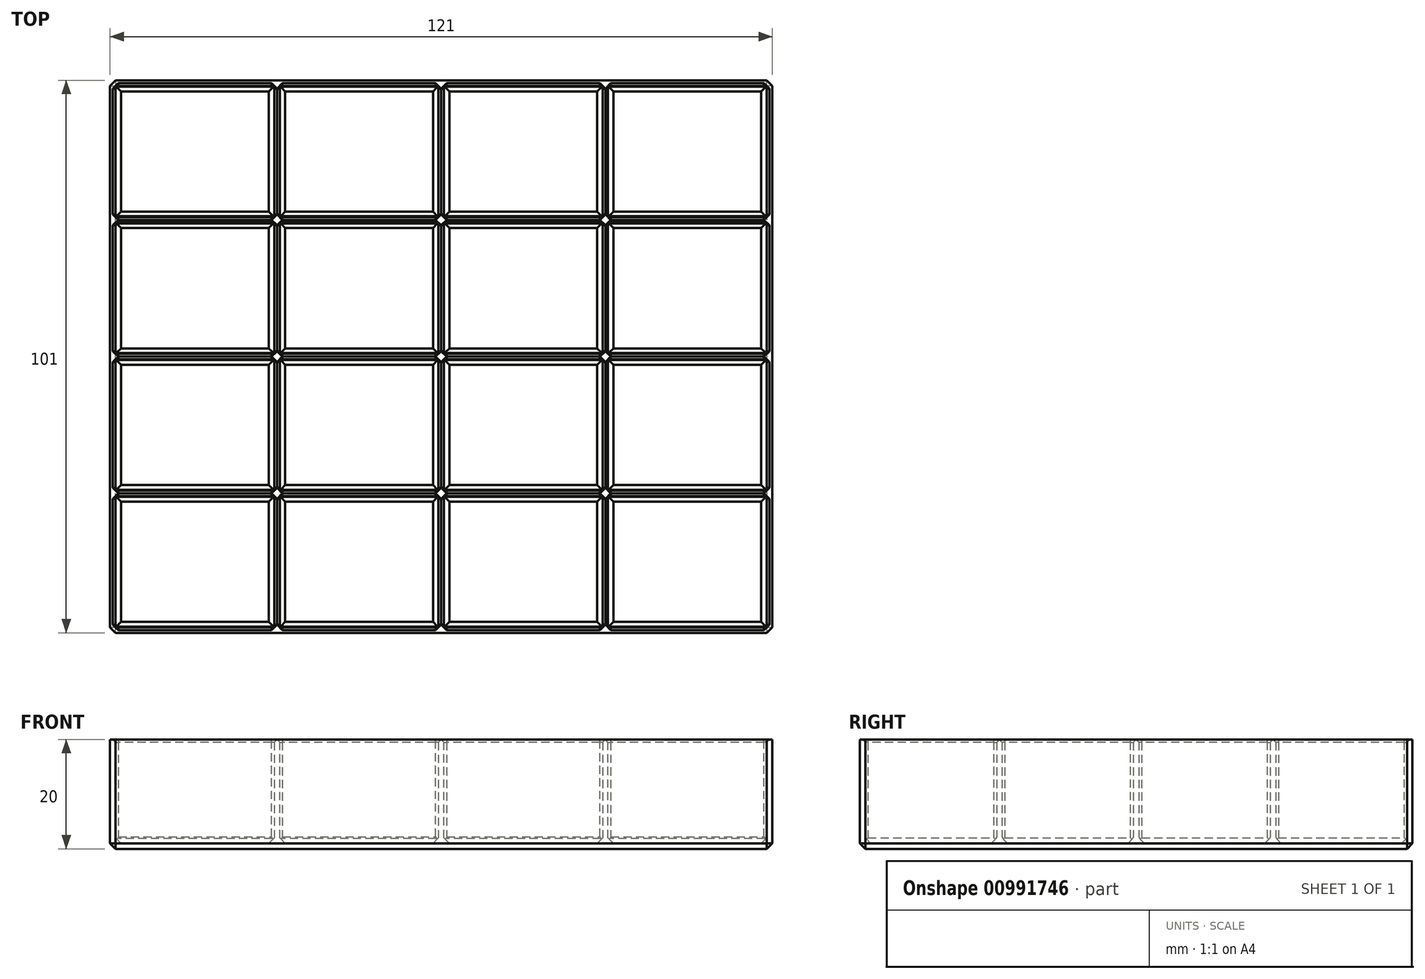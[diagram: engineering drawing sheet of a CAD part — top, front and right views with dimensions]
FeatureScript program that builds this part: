
annotation { "Feature Type Name" : "Feature", "Feature Type Description" : "" }
export const myFeature = defineFeature(function(context is Context, id is Id, definition is map)
    precondition{}
    {
        {
            var Q0;
            Q0=qCreatedBy(makeId("Top.planeOp"),FACE);
            var sketch = newSketch(context, id + "F0", { "sketchPlane" : qUnion([Q0])});
            skLineSegment(sketch, "E0.bottom", {"start": v(-60, 50) * mm, "end": v(60, 50) * mm, "construction": true});
            skLineSegment(sketch, "E0.top", {"start": v(-60, -50) * mm, "end": v(60, -50) * mm, "construction": true});
            skLineSegment(sketch, "E0.left", {"start": v(-60, 50) * mm, "end": v(-60, -50) * mm, "construction": true});
            skLineSegment(sketch, "E0.right", {"start": v(60, 50) * mm, "end": v(60, -50) * mm, "construction": true});
            skLineSegment(sketch, "E1", {"start": v(0, 50) * mm, "end": v(0, -50) * mm, "construction": true});
            skLineSegment(sketch, "E2", {"start": v(-60, 0) * mm, "end": v(60, 0) * mm, "construction": true});
            skLineSegment(sketch, "E3", {"start": v(-30, 50) * mm, "end": v(-30, -50) * mm, "construction": true});
            skLineSegment(sketch, "E4", {"start": v(30, 50) * mm, "end": v(30, -50) * mm, "construction": true});
            skLineSegment(sketch, "E5", {"start": v(60, -25) * mm, "end": v(-60, -25) * mm, "construction": true});
            skLineSegment(sketch, "E6", {"start": v(60, 25) * mm, "end": v(-60, 25) * mm, "construction": true});
            skLineSegment(sketch, "E7.bottom", {"start": v(-59.5, 49.5) * mm, "end": v(-30.5, 49.5) * mm});
            skLineSegment(sketch, "E7.top", {"start": v(-59.5, 25.5) * mm, "end": v(-30.5, 25.5) * mm});
            skLineSegment(sketch, "E7.left", {"start": v(-59.5, 49.5) * mm, "end": v(-59.5, 25.5) * mm});
            skLineSegment(sketch, "E7.right", {"start": v(-30.5, 49.5) * mm, "end": v(-30.5, 25.5) * mm});
            skLineSegment(sketch, "E8.0.1.0", {"start": v(-59.5, 24.5) * mm, "end": v(-30.5, 24.5) * mm});
            skLineSegment(sketch, "E8.0.1.1", {"start": v(-59.5, 24.5) * mm, "end": v(-59.5, 0.5) * mm});
            skLineSegment(sketch, "E8.0.1.2", {"start": v(-59.5, 0.5) * mm, "end": v(-30.5, 0.5) * mm});
            skLineSegment(sketch, "E8.0.1.3", {"start": v(-30.5, 24.5) * mm, "end": v(-30.5, 0.5) * mm});
            skLineSegment(sketch, "E8.0.2.0", {"start": v(-59.5, -0.5) * mm, "end": v(-30.5, -0.5) * mm});
            skLineSegment(sketch, "E8.0.2.1", {"start": v(-59.5, -0.5) * mm, "end": v(-59.5, -24.5) * mm});
            skLineSegment(sketch, "E8.0.2.2", {"start": v(-59.5, -24.5) * mm, "end": v(-30.5, -24.5) * mm});
            skLineSegment(sketch, "E8.0.2.3", {"start": v(-30.5, -0.5) * mm, "end": v(-30.5, -24.5) * mm});
            skLineSegment(sketch, "E8.0.3.0", {"start": v(-59.5, -25.5) * mm, "end": v(-30.5, -25.5) * mm});
            skLineSegment(sketch, "E8.0.3.1", {"start": v(-59.5, -25.5) * mm, "end": v(-59.5, -49.5) * mm});
            skLineSegment(sketch, "E8.0.3.2", {"start": v(-59.5, -49.5) * mm, "end": v(-30.5, -49.5) * mm});
            skLineSegment(sketch, "E8.0.3.3", {"start": v(-30.5, -25.5) * mm, "end": v(-30.5, -49.5) * mm});
            skLineSegment(sketch, "E8.1.0.0", {"start": v(-29.5, 49.5) * mm, "end": v(-0.5, 49.5) * mm});
            skLineSegment(sketch, "E8.1.0.1", {"start": v(-29.5, 49.5) * mm, "end": v(-29.5, 25.5) * mm});
            skLineSegment(sketch, "E8.1.0.2", {"start": v(-29.5, 25.5) * mm, "end": v(-0.5, 25.5) * mm});
            skLineSegment(sketch, "E8.1.0.3", {"start": v(-0.5, 49.5) * mm, "end": v(-0.5, 25.5) * mm});
            skLineSegment(sketch, "E8.1.1.0", {"start": v(-29.5, 24.5) * mm, "end": v(-0.5, 24.5) * mm});
            skLineSegment(sketch, "E8.1.1.1", {"start": v(-29.5, 24.5) * mm, "end": v(-29.5, 0.5) * mm});
            skLineSegment(sketch, "E8.1.1.2", {"start": v(-29.5, 0.5) * mm, "end": v(-0.5, 0.5) * mm});
            skLineSegment(sketch, "E8.1.1.3", {"start": v(-0.5, 24.5) * mm, "end": v(-0.5, 0.5) * mm});
            skLineSegment(sketch, "E8.1.2.0", {"start": v(-29.5, -0.5) * mm, "end": v(-0.5, -0.5) * mm});
            skLineSegment(sketch, "E8.1.2.1", {"start": v(-29.5, -0.5) * mm, "end": v(-29.5, -24.5) * mm});
            skLineSegment(sketch, "E8.1.2.2", {"start": v(-29.5, -24.5) * mm, "end": v(-0.5, -24.5) * mm});
            skLineSegment(sketch, "E8.1.2.3", {"start": v(-0.5, -0.5) * mm, "end": v(-0.5, -24.5) * mm});
            skLineSegment(sketch, "E8.1.3.0", {"start": v(-29.5, -25.5) * mm, "end": v(-0.5, -25.5) * mm});
            skLineSegment(sketch, "E8.1.3.1", {"start": v(-29.5, -25.5) * mm, "end": v(-29.5, -49.5) * mm});
            skLineSegment(sketch, "E8.1.3.2", {"start": v(-29.5, -49.5) * mm, "end": v(-0.5, -49.5) * mm});
            skLineSegment(sketch, "E8.1.3.3", {"start": v(-0.5, -25.5) * mm, "end": v(-0.5, -49.5) * mm});
            skLineSegment(sketch, "E8.2.0.0", {"start": v(0.5, 49.5) * mm, "end": v(29.5, 49.5) * mm});
            skLineSegment(sketch, "E8.2.0.1", {"start": v(0.5, 49.5) * mm, "end": v(0.5, 25.5) * mm});
            skLineSegment(sketch, "E8.2.0.2", {"start": v(0.5, 25.5) * mm, "end": v(29.5, 25.5) * mm});
            skLineSegment(sketch, "E8.2.0.3", {"start": v(29.5, 49.5) * mm, "end": v(29.5, 25.5) * mm});
            skLineSegment(sketch, "E8.2.1.0", {"start": v(0.5, 24.5) * mm, "end": v(29.5, 24.5) * mm});
            skLineSegment(sketch, "E8.2.1.1", {"start": v(0.5, 24.5) * mm, "end": v(0.5, 0.5) * mm});
            skLineSegment(sketch, "E8.2.1.2", {"start": v(0.5, 0.5) * mm, "end": v(29.5, 0.5) * mm});
            skLineSegment(sketch, "E8.2.1.3", {"start": v(29.5, 24.5) * mm, "end": v(29.5, 0.5) * mm});
            skLineSegment(sketch, "E8.2.2.0", {"start": v(0.5, -0.5) * mm, "end": v(29.5, -0.5) * mm});
            skLineSegment(sketch, "E8.2.2.1", {"start": v(0.5, -0.5) * mm, "end": v(0.5, -24.5) * mm});
            skLineSegment(sketch, "E8.2.2.2", {"start": v(0.5, -24.5) * mm, "end": v(29.5, -24.5) * mm});
            skLineSegment(sketch, "E8.2.2.3", {"start": v(29.5, -0.5) * mm, "end": v(29.5, -24.5) * mm});
            skLineSegment(sketch, "E8.2.3.0", {"start": v(0.5, -25.5) * mm, "end": v(29.5, -25.5) * mm});
            skLineSegment(sketch, "E8.2.3.1", {"start": v(0.5, -25.5) * mm, "end": v(0.5, -49.5) * mm});
            skLineSegment(sketch, "E8.2.3.2", {"start": v(0.5, -49.5) * mm, "end": v(29.5, -49.5) * mm});
            skLineSegment(sketch, "E8.2.3.3", {"start": v(29.5, -25.5) * mm, "end": v(29.5, -49.5) * mm});
            skLineSegment(sketch, "E8.3.0.0", {"start": v(30.5, 49.5) * mm, "end": v(59.5, 49.5) * mm});
            skLineSegment(sketch, "E8.3.0.1", {"start": v(30.5, 49.5) * mm, "end": v(30.5, 25.5) * mm});
            skLineSegment(sketch, "E8.3.0.2", {"start": v(30.5, 25.5) * mm, "end": v(59.5, 25.5) * mm});
            skLineSegment(sketch, "E8.3.0.3", {"start": v(59.5, 49.5) * mm, "end": v(59.5, 25.5) * mm});
            skLineSegment(sketch, "E8.3.1.0", {"start": v(30.5, 24.5) * mm, "end": v(59.5, 24.5) * mm});
            skLineSegment(sketch, "E8.3.1.1", {"start": v(30.5, 24.5) * mm, "end": v(30.5, 0.5) * mm});
            skLineSegment(sketch, "E8.3.1.2", {"start": v(30.5, 0.5) * mm, "end": v(59.5, 0.5) * mm});
            skLineSegment(sketch, "E8.3.1.3", {"start": v(59.5, 24.5) * mm, "end": v(59.5, 0.5) * mm});
            skLineSegment(sketch, "E8.3.2.0", {"start": v(30.5, -0.5) * mm, "end": v(59.5, -0.5) * mm});
            skLineSegment(sketch, "E8.3.2.1", {"start": v(30.5, -0.5) * mm, "end": v(30.5, -24.5) * mm});
            skLineSegment(sketch, "E8.3.2.2", {"start": v(30.5, -24.5) * mm, "end": v(59.5, -24.5) * mm});
            skLineSegment(sketch, "E8.3.2.3", {"start": v(59.5, -0.5) * mm, "end": v(59.5, -24.5) * mm});
            skLineSegment(sketch, "E8.3.3.0", {"start": v(30.5, -25.5) * mm, "end": v(59.5, -25.5) * mm});
            skLineSegment(sketch, "E8.3.3.1", {"start": v(30.5, -25.5) * mm, "end": v(30.5, -49.5) * mm});
            skLineSegment(sketch, "E8.3.3.2", {"start": v(30.5, -49.5) * mm, "end": v(59.5, -49.5) * mm});
            skLineSegment(sketch, "E8.3.3.3", {"start": v(59.5, -25.5) * mm, "end": v(59.5, -49.5) * mm});
            skLineSegment(sketch, "E8.direction1", {"start": v(-59.5, 25.5) * mm, "end": v(-29.5, 25.5) * mm, "construction": true});
            skLineSegment(sketch, "E8.direction2", {"start": v(-59.5, 25.5) * mm, "end": v(-59.5, 0.5) * mm, "construction": true});
            skLineSegment(sketch, "E9.bottom", {"start": v(-60.5, 50.5) * mm, "end": v(60.5, 50.5) * mm});
            skLineSegment(sketch, "E9.top", {"start": v(-60.5, -50.5) * mm, "end": v(60.5, -50.5) * mm});
            skLineSegment(sketch, "E9.left", {"start": v(-60.5, 50.5) * mm, "end": v(-60.5, -50.5) * mm});
            skLineSegment(sketch, "E9.right", {"start": v(60.5, 50.5) * mm, "end": v(60.5, -50.5) * mm});
            skSolve(sketch);
        }
        {
            var Q0;
            Q0 = qSketchRegion(id + "F0", true);
            extrude(context, id + "F1", {"entities" : qUnion([Q0]), "depth" : 19 * mm, "offsetDistance" : 25 * mm});
        }
        {
            var Q0;
            Q0=makeQuery(id+"F0.imprint","IMPRINT",FACE,{"disambiguationData":[TD([[makeQuery(id+"F0.imprint","IMPRINT",EDGE,{"derivedFrom":sQuery(id+"F0.wireOp",EDGE,"E8.0.3.0")}),-1.0]])]});
            var Q1;
            Q1=makeQuery(id+"F0.imprint","IMPRINT",FACE,{"disambiguationData":[TD([[makeQuery(id+"F0.imprint","IMPRINT",EDGE,{"derivedFrom":sQuery(id+"F0.wireOp",EDGE,"E8.1.3.0")}),-1.0]])]});
            var Q2;
            Q2=makeQuery(id+"F0.imprint","IMPRINT",FACE,{"disambiguationData":[TD([[makeQuery(id+"F0.imprint","IMPRINT",EDGE,{"derivedFrom":sQuery(id+"F0.wireOp",EDGE,"E8.2.3.0")}),-1.0]])]});
            var Q3;
            Q3=makeQuery(id+"F0.imprint","IMPRINT",FACE,{"disambiguationData":[TD([[makeQuery(id+"F0.imprint","IMPRINT",EDGE,{"derivedFrom":sQuery(id+"F0.wireOp",EDGE,"E8.3.3.0")}),-1.0]])]});
            var Q4;
            Q4=makeQuery(id+"F0.imprint","IMPRINT",FACE,{"disambiguationData":[TD([[makeQuery(id+"F0.imprint","IMPRINT",EDGE,{"derivedFrom":sQuery(id+"F0.wireOp",EDGE,"E8.3.2.0")}),-1.0]])]});
            var Q5;
            Q5=makeQuery(id+"F0.imprint","IMPRINT",FACE,{"disambiguationData":[TD([[makeQuery(id+"F0.imprint","IMPRINT",EDGE,{"derivedFrom":sQuery(id+"F0.wireOp",EDGE,"E8.2.2.0")}),-1.0]])]});
            var Q6;
            Q6=makeQuery(id+"F0.imprint","IMPRINT",FACE,{"disambiguationData":[TD([[makeQuery(id+"F0.imprint","IMPRINT",EDGE,{"derivedFrom":sQuery(id+"F0.wireOp",EDGE,"E8.1.2.0")}),-1.0]])]});
            var Q7;
            Q7=makeQuery(id+"F0.imprint","IMPRINT",FACE,{"disambiguationData":[TD([[makeQuery(id+"F0.imprint","IMPRINT",EDGE,{"derivedFrom":sQuery(id+"F0.wireOp",EDGE,"E8.0.2.0")}),-1.0]])]});
            var Q8;
            Q8=makeQuery(id+"F0.imprint","IMPRINT",FACE,{"disambiguationData":[TD([[makeQuery(id+"F0.imprint","IMPRINT",EDGE,{"derivedFrom":sQuery(id+"F0.wireOp",EDGE,"E8.0.1.0")}),-1.0]])]});
            var Q9;
            Q9=makeQuery(id+"F0.imprint","IMPRINT",FACE,{"disambiguationData":[TD([[makeQuery(id+"F0.imprint","IMPRINT",EDGE,{"derivedFrom":sQuery(id+"F0.wireOp",EDGE,"E8.1.1.0")}),-1.0]])]});
            var Q10;
            Q10=makeQuery(id+"F0.imprint","IMPRINT",FACE,{"disambiguationData":[TD([[makeQuery(id+"F0.imprint","IMPRINT",EDGE,{"derivedFrom":sQuery(id+"F0.wireOp",EDGE,"E8.2.1.0")}),-1.0]])]});
            var Q11;
            Q11=makeQuery(id+"F0.imprint","IMPRINT",FACE,{"disambiguationData":[TD([[makeQuery(id+"F0.imprint","IMPRINT",EDGE,{"derivedFrom":sQuery(id+"F0.wireOp",EDGE,"E8.3.1.0")}),-1.0]])]});
            var Q12;
            Q12=makeQuery(id+"F0.imprint","IMPRINT",FACE,{"disambiguationData":[TD([[makeQuery(id+"F0.imprint","IMPRINT",EDGE,{"derivedFrom":sQuery(id+"F0.wireOp",EDGE,"E8.3.0.0")}),-1.0]])]});
            var Q13;
            Q13=makeQuery(id+"F0.imprint","IMPRINT",FACE,{"disambiguationData":[TD([[makeQuery(id+"F0.imprint","IMPRINT",EDGE,{"derivedFrom":sQuery(id+"F0.wireOp",EDGE,"E8.2.0.0")}),-1.0]])]});
            var Q14;
            Q14=makeQuery(id+"F0.imprint","IMPRINT",FACE,{"disambiguationData":[TD([[makeQuery(id+"F0.imprint","IMPRINT",EDGE,{"derivedFrom":sQuery(id+"F0.wireOp",EDGE,"E8.1.0.0")}),-1.0]])]});
            var Q15;
            Q15=makeQuery(id+"F0.imprint","IMPRINT",FACE,{"disambiguationData":[TD([[makeQuery(id+"F0.imprint","IMPRINT",EDGE,{"derivedFrom":sQuery(id+"F0.wireOp",EDGE,"E7.bottom")}),-1.0]])]});
            var Q16;
            Q16=makeQuery(id+"F0.imprint","IMPRINT",FACE,{"disambiguationData":[TD([[makeQuery(id+"F0.imprint","IMPRINT",EDGE,{"derivedFrom":sQuery(id+"F0.wireOp",EDGE,"E7.bottom")}),1.0]])]});
            extrude(context, id + "F2", {"entities" : qUnion([Q0, Q1, Q2, Q3, Q4, Q5, Q6, Q7, Q8, Q9, Q10, Q11, Q12, Q13, Q14, Q15, Q16]), "operationType" : NewBodyOperationType.ADD, "oppositeDirection" : true, "depth" : 1 * mm, "offsetDistance" : 25 * mm});
        }
        {
            var Q0;
            Q0=makeQuery(id+"F2.opExtrude","CAP_EDGE",EDGE,{"disambiguationData":[OSD([sQuery(id+"F0.wireOp",EDGE,"E9.top")])],"isStart":false});
            var Q1;
            Q1=makeQuery(id+"F2.opExtrude","CAP_EDGE",EDGE,{"disambiguationData":[OSD([sQuery(id+"F0.wireOp",EDGE,"E9.left")])],"isStart":false});
            var Q2;
            Q2=makeQuery(id+"F2.opExtrude","CAP_EDGE",EDGE,{"disambiguationData":[OSD([sQuery(id+"F0.wireOp",EDGE,"E9.right")])],"isStart":false});
            var Q3;
            Q3=makeQuery(id+"F2.opExtrude","CAP_EDGE",EDGE,{"disambiguationData":[OSD([sQuery(id+"F0.wireOp",EDGE,"E9.bottom")])],"isStart":false});
            var Q4;
            {var subQ0=sQuery(id+"F0.wireOp",EDGE,"E9.right");var subQ1=sQuery(id+"F0.wireOp",EDGE,"E9.top");Q4=makeQuery(id+"F2.boolean.opBoolean","MERGE",EDGE,{"derivedFrom":[makeQuery(id+"F1.opExtrude","SWEPT_EDGE",EDGE,{"disambiguationData":[OSD([subQ1,subQ0])]}),makeQuery(id+"F2.opExtrude","SWEPT_EDGE",EDGE,{"disambiguationData":[OSD([subQ1,subQ0])]})]});}
            var Q5;
            {var subQ0=sQuery(id+"F0.wireOp",EDGE,"E9.left");var subQ1=sQuery(id+"F0.wireOp",EDGE,"E9.top");Q5=makeQuery(id+"F2.boolean.opBoolean","MERGE",EDGE,{"derivedFrom":[makeQuery(id+"F1.opExtrude","SWEPT_EDGE",EDGE,{"disambiguationData":[OSD([subQ1,subQ0])]}),makeQuery(id+"F2.opExtrude","SWEPT_EDGE",EDGE,{"disambiguationData":[OSD([subQ1,subQ0])]})]});}
            var Q6;
            {var subQ0=sQuery(id+"F0.wireOp",EDGE,"E9.left");var subQ1=sQuery(id+"F0.wireOp",EDGE,"E9.bottom");Q6=makeQuery(id+"F2.boolean.opBoolean","MERGE",EDGE,{"derivedFrom":[makeQuery(id+"F1.opExtrude","SWEPT_EDGE",EDGE,{"disambiguationData":[OSD([subQ1,subQ0])]}),makeQuery(id+"F2.opExtrude","SWEPT_EDGE",EDGE,{"disambiguationData":[OSD([subQ1,subQ0])]})]});}
            var Q7;
            {var subQ0=sQuery(id+"F0.wireOp",EDGE,"E9.right");var subQ1=sQuery(id+"F0.wireOp",EDGE,"E9.bottom");Q7=makeQuery(id+"F2.boolean.opBoolean","MERGE",EDGE,{"derivedFrom":[makeQuery(id+"F1.opExtrude","SWEPT_EDGE",EDGE,{"disambiguationData":[OSD([subQ1,subQ0])]}),makeQuery(id+"F2.opExtrude","SWEPT_EDGE",EDGE,{"disambiguationData":[OSD([subQ1,subQ0])]})]});}
            chamfer(context, id + "F3", {"entities" : qUnion([Q0, Q1, Q2, Q3, Q4, Q5, Q6, Q7]), "width" : 1 * mm, "tangentPropagation" : true});
        }
        {
            var Q0;
            Q0=makeQuery(id+"F2.boolean.opBoolean","SPLIT",FACE,{"disambiguationData":[TD([makeQuery(id+"F1.opExtrude","SWEPT_FACE",FACE,{"disambiguationData":[OSD([sQuery(id+"F0.wireOp",EDGE,"E7.bottom")])]})])],"derivedFrom":makeQuery(id+"F2.opExtrude","CAP_FACE",FACE,{"disambiguationData":[OSD([sQuery(id+"F0.wireOp",EDGE,"E9.bottom"),sQuery(id+"F0.wireOp",EDGE,"E9.top"),sQuery(id+"F0.wireOp",EDGE,"E9.left"),sQuery(id+"F0.wireOp",EDGE,"E9.right")])],"isStart":true})});
            var Q1;
            Q1=makeQuery(id+"F2.boolean.opBoolean","SPLIT",FACE,{"disambiguationData":[TD([makeQuery(id+"F1.opExtrude","SWEPT_FACE",FACE,{"disambiguationData":[OSD([sQuery(id+"F0.wireOp",EDGE,"E8.1.0.0")])]})])],"derivedFrom":makeQuery(id+"F2.opExtrude","CAP_FACE",FACE,{"disambiguationData":[OSD([sQuery(id+"F0.wireOp",EDGE,"E9.bottom"),sQuery(id+"F0.wireOp",EDGE,"E9.top"),sQuery(id+"F0.wireOp",EDGE,"E9.left"),sQuery(id+"F0.wireOp",EDGE,"E9.right")])],"isStart":true})});
            var Q2;
            Q2=makeQuery(id+"F2.boolean.opBoolean","SPLIT",FACE,{"disambiguationData":[TD([makeQuery(id+"F1.opExtrude","SWEPT_FACE",FACE,{"disambiguationData":[OSD([sQuery(id+"F0.wireOp",EDGE,"E8.2.0.0")])]})])],"derivedFrom":makeQuery(id+"F2.opExtrude","CAP_FACE",FACE,{"disambiguationData":[OSD([sQuery(id+"F0.wireOp",EDGE,"E9.bottom"),sQuery(id+"F0.wireOp",EDGE,"E9.top"),sQuery(id+"F0.wireOp",EDGE,"E9.left"),sQuery(id+"F0.wireOp",EDGE,"E9.right")])],"isStart":true})});
            var Q3;
            Q3=makeQuery(id+"F2.boolean.opBoolean","SPLIT",FACE,{"disambiguationData":[TD([makeQuery(id+"F1.opExtrude","SWEPT_FACE",FACE,{"disambiguationData":[OSD([sQuery(id+"F0.wireOp",EDGE,"E8.3.0.0")])]})])],"derivedFrom":makeQuery(id+"F2.opExtrude","CAP_FACE",FACE,{"disambiguationData":[OSD([sQuery(id+"F0.wireOp",EDGE,"E9.bottom"),sQuery(id+"F0.wireOp",EDGE,"E9.top"),sQuery(id+"F0.wireOp",EDGE,"E9.left"),sQuery(id+"F0.wireOp",EDGE,"E9.right")])],"isStart":true})});
            var Q4;
            Q4=makeQuery(id+"F2.boolean.opBoolean","SPLIT",FACE,{"disambiguationData":[TD([makeQuery(id+"F1.opExtrude","SWEPT_FACE",FACE,{"disambiguationData":[OSD([sQuery(id+"F0.wireOp",EDGE,"E8.3.1.0")])]})])],"derivedFrom":makeQuery(id+"F2.opExtrude","CAP_FACE",FACE,{"disambiguationData":[OSD([sQuery(id+"F0.wireOp",EDGE,"E9.bottom"),sQuery(id+"F0.wireOp",EDGE,"E9.top"),sQuery(id+"F0.wireOp",EDGE,"E9.left"),sQuery(id+"F0.wireOp",EDGE,"E9.right")])],"isStart":true})});
            var Q5;
            Q5=makeQuery(id+"F2.boolean.opBoolean","SPLIT",FACE,{"disambiguationData":[TD([makeQuery(id+"F1.opExtrude","SWEPT_FACE",FACE,{"disambiguationData":[OSD([sQuery(id+"F0.wireOp",EDGE,"E8.3.2.0")])]})])],"derivedFrom":makeQuery(id+"F2.opExtrude","CAP_FACE",FACE,{"disambiguationData":[OSD([sQuery(id+"F0.wireOp",EDGE,"E9.bottom"),sQuery(id+"F0.wireOp",EDGE,"E9.top"),sQuery(id+"F0.wireOp",EDGE,"E9.left"),sQuery(id+"F0.wireOp",EDGE,"E9.right")])],"isStart":true})});
            var Q6;
            Q6=makeQuery(id+"F2.boolean.opBoolean","SPLIT",FACE,{"disambiguationData":[TD([makeQuery(id+"F1.opExtrude","SWEPT_FACE",FACE,{"disambiguationData":[OSD([sQuery(id+"F0.wireOp",EDGE,"E8.3.3.0")])]})])],"derivedFrom":makeQuery(id+"F2.opExtrude","CAP_FACE",FACE,{"disambiguationData":[OSD([sQuery(id+"F0.wireOp",EDGE,"E9.bottom"),sQuery(id+"F0.wireOp",EDGE,"E9.top"),sQuery(id+"F0.wireOp",EDGE,"E9.left"),sQuery(id+"F0.wireOp",EDGE,"E9.right")])],"isStart":true})});
            var Q7;
            Q7=makeQuery(id+"F2.boolean.opBoolean","SPLIT",FACE,{"disambiguationData":[TD([makeQuery(id+"F1.opExtrude","SWEPT_FACE",FACE,{"disambiguationData":[OSD([sQuery(id+"F0.wireOp",EDGE,"E8.2.3.0")])]})])],"derivedFrom":makeQuery(id+"F2.opExtrude","CAP_FACE",FACE,{"disambiguationData":[OSD([sQuery(id+"F0.wireOp",EDGE,"E9.bottom"),sQuery(id+"F0.wireOp",EDGE,"E9.top"),sQuery(id+"F0.wireOp",EDGE,"E9.left"),sQuery(id+"F0.wireOp",EDGE,"E9.right")])],"isStart":true})});
            var Q8;
            Q8=makeQuery(id+"F2.boolean.opBoolean","SPLIT",FACE,{"disambiguationData":[TD([makeQuery(id+"F1.opExtrude","SWEPT_FACE",FACE,{"disambiguationData":[OSD([sQuery(id+"F0.wireOp",EDGE,"E8.2.2.0")])]})])],"derivedFrom":makeQuery(id+"F2.opExtrude","CAP_FACE",FACE,{"disambiguationData":[OSD([sQuery(id+"F0.wireOp",EDGE,"E9.bottom"),sQuery(id+"F0.wireOp",EDGE,"E9.top"),sQuery(id+"F0.wireOp",EDGE,"E9.left"),sQuery(id+"F0.wireOp",EDGE,"E9.right")])],"isStart":true})});
            var Q9;
            Q9=makeQuery(id+"F2.boolean.opBoolean","SPLIT",FACE,{"disambiguationData":[TD([makeQuery(id+"F1.opExtrude","SWEPT_FACE",FACE,{"disambiguationData":[OSD([sQuery(id+"F0.wireOp",EDGE,"E8.2.1.0")])]})])],"derivedFrom":makeQuery(id+"F2.opExtrude","CAP_FACE",FACE,{"disambiguationData":[OSD([sQuery(id+"F0.wireOp",EDGE,"E9.bottom"),sQuery(id+"F0.wireOp",EDGE,"E9.top"),sQuery(id+"F0.wireOp",EDGE,"E9.left"),sQuery(id+"F0.wireOp",EDGE,"E9.right")])],"isStart":true})});
            var Q10;
            Q10=makeQuery(id+"F2.boolean.opBoolean","SPLIT",FACE,{"disambiguationData":[TD([makeQuery(id+"F1.opExtrude","SWEPT_FACE",FACE,{"disambiguationData":[OSD([sQuery(id+"F0.wireOp",EDGE,"E8.1.1.0")])]})])],"derivedFrom":makeQuery(id+"F2.opExtrude","CAP_FACE",FACE,{"disambiguationData":[OSD([sQuery(id+"F0.wireOp",EDGE,"E9.bottom"),sQuery(id+"F0.wireOp",EDGE,"E9.top"),sQuery(id+"F0.wireOp",EDGE,"E9.left"),sQuery(id+"F0.wireOp",EDGE,"E9.right")])],"isStart":true})});
            var Q11;
            Q11=makeQuery(id+"F2.boolean.opBoolean","SPLIT",FACE,{"disambiguationData":[TD([makeQuery(id+"F1.opExtrude","SWEPT_FACE",FACE,{"disambiguationData":[OSD([sQuery(id+"F0.wireOp",EDGE,"E8.1.2.0")])]})])],"derivedFrom":makeQuery(id+"F2.opExtrude","CAP_FACE",FACE,{"disambiguationData":[OSD([sQuery(id+"F0.wireOp",EDGE,"E9.bottom"),sQuery(id+"F0.wireOp",EDGE,"E9.top"),sQuery(id+"F0.wireOp",EDGE,"E9.left"),sQuery(id+"F0.wireOp",EDGE,"E9.right")])],"isStart":true})});
            var Q12;
            Q12=makeQuery(id+"F2.boolean.opBoolean","SPLIT",FACE,{"disambiguationData":[TD([makeQuery(id+"F1.opExtrude","SWEPT_FACE",FACE,{"disambiguationData":[OSD([sQuery(id+"F0.wireOp",EDGE,"E8.0.1.0")])]})])],"derivedFrom":makeQuery(id+"F2.opExtrude","CAP_FACE",FACE,{"disambiguationData":[OSD([sQuery(id+"F0.wireOp",EDGE,"E9.bottom"),sQuery(id+"F0.wireOp",EDGE,"E9.top"),sQuery(id+"F0.wireOp",EDGE,"E9.left"),sQuery(id+"F0.wireOp",EDGE,"E9.right")])],"isStart":true})});
            var Q13;
            Q13=makeQuery(id+"F2.boolean.opBoolean","SPLIT",FACE,{"disambiguationData":[TD([makeQuery(id+"F1.opExtrude","SWEPT_FACE",FACE,{"disambiguationData":[OSD([sQuery(id+"F0.wireOp",EDGE,"E8.0.2.0")])]})])],"derivedFrom":makeQuery(id+"F2.opExtrude","CAP_FACE",FACE,{"disambiguationData":[OSD([sQuery(id+"F0.wireOp",EDGE,"E9.bottom"),sQuery(id+"F0.wireOp",EDGE,"E9.top"),sQuery(id+"F0.wireOp",EDGE,"E9.left"),sQuery(id+"F0.wireOp",EDGE,"E9.right")])],"isStart":true})});
            var Q14;
            Q14=makeQuery(id+"F2.boolean.opBoolean","SPLIT",FACE,{"disambiguationData":[TD([makeQuery(id+"F1.opExtrude","SWEPT_FACE",FACE,{"disambiguationData":[OSD([sQuery(id+"F0.wireOp",EDGE,"E8.0.3.0")])]})])],"derivedFrom":makeQuery(id+"F2.opExtrude","CAP_FACE",FACE,{"disambiguationData":[OSD([sQuery(id+"F0.wireOp",EDGE,"E9.bottom"),sQuery(id+"F0.wireOp",EDGE,"E9.top"),sQuery(id+"F0.wireOp",EDGE,"E9.left"),sQuery(id+"F0.wireOp",EDGE,"E9.right")])],"isStart":true})});
            var Q15;
            Q15=makeQuery(id+"F2.boolean.opBoolean","SPLIT",FACE,{"disambiguationData":[TD([makeQuery(id+"F1.opExtrude","SWEPT_FACE",FACE,{"disambiguationData":[OSD([sQuery(id+"F0.wireOp",EDGE,"E8.1.3.0")])]})])],"derivedFrom":makeQuery(id+"F2.opExtrude","CAP_FACE",FACE,{"disambiguationData":[OSD([sQuery(id+"F0.wireOp",EDGE,"E9.bottom"),sQuery(id+"F0.wireOp",EDGE,"E9.top"),sQuery(id+"F0.wireOp",EDGE,"E9.left"),sQuery(id+"F0.wireOp",EDGE,"E9.right")])],"isStart":true})});
            chamfer(context, id + "F4", {"entities" : qUnion([Q0, Q1, Q2, Q3, Q4, Q5, Q6, Q7, Q8, Q9, Q10, Q11, Q12, Q13, Q14, Q15]), "width" : 1 * mm, "tangentPropagation" : true});
        }
        {
            var Q0;
            Q0=makeQuery(id+"F1.opExtrude","SWEPT_FACE",FACE,{"disambiguationData":[OSD([sQuery(id+"F0.wireOp",EDGE,"E7.bottom")])]});
            var Q1;
            Q1=makeQuery(id+"F1.opExtrude","SWEPT_FACE",FACE,{"disambiguationData":[OSD([sQuery(id+"F0.wireOp",EDGE,"E7.top")])]});
            var Q2;
            Q2=makeQuery(id+"F1.opExtrude","SWEPT_FACE",FACE,{"disambiguationData":[OSD([sQuery(id+"F0.wireOp",EDGE,"E8.0.1.2")])]});
            var Q3;
            Q3=makeQuery(id+"F1.opExtrude","SWEPT_FACE",FACE,{"disambiguationData":[OSD([sQuery(id+"F0.wireOp",EDGE,"E8.0.1.0")])]});
            var Q4;
            Q4=makeQuery(id+"F1.opExtrude","SWEPT_FACE",FACE,{"disambiguationData":[OSD([sQuery(id+"F0.wireOp",EDGE,"E8.0.2.0")])]});
            var Q5;
            Q5=makeQuery(id+"F1.opExtrude","SWEPT_FACE",FACE,{"disambiguationData":[OSD([sQuery(id+"F0.wireOp",EDGE,"E8.0.2.2")])]});
            var Q6;
            Q6=makeQuery(id+"F1.opExtrude","SWEPT_FACE",FACE,{"disambiguationData":[OSD([sQuery(id+"F0.wireOp",EDGE,"E8.0.3.0")])]});
            var Q7;
            Q7=makeQuery(id+"F1.opExtrude","SWEPT_FACE",FACE,{"disambiguationData":[OSD([sQuery(id+"F0.wireOp",EDGE,"E8.0.3.2")])]});
            var Q8;
            Q8=makeQuery(id+"F1.opExtrude","SWEPT_FACE",FACE,{"disambiguationData":[OSD([sQuery(id+"F0.wireOp",EDGE,"E8.1.3.2")])]});
            var Q9;
            Q9=makeQuery(id+"F1.opExtrude","SWEPT_FACE",FACE,{"disambiguationData":[OSD([sQuery(id+"F0.wireOp",EDGE,"E8.2.3.2")])]});
            var Q10;
            Q10=makeQuery(id+"F1.opExtrude","SWEPT_FACE",FACE,{"disambiguationData":[OSD([sQuery(id+"F0.wireOp",EDGE,"E8.3.3.2")])]});
            var Q11;
            Q11=makeQuery(id+"F1.opExtrude","SWEPT_FACE",FACE,{"disambiguationData":[OSD([sQuery(id+"F0.wireOp",EDGE,"E8.3.2.2")])]});
            var Q12;
            Q12=makeQuery(id+"F1.opExtrude","SWEPT_FACE",FACE,{"disambiguationData":[OSD([sQuery(id+"F0.wireOp",EDGE,"E8.2.2.2")])]});
            var Q13;
            Q13=makeQuery(id+"F1.opExtrude","SWEPT_FACE",FACE,{"disambiguationData":[OSD([sQuery(id+"F0.wireOp",EDGE,"E8.1.2.2")])]});
            var Q14;
            Q14=makeQuery(id+"F1.opExtrude","SWEPT_FACE",FACE,{"disambiguationData":[OSD([sQuery(id+"F0.wireOp",EDGE,"E8.1.1.2")])]});
            var Q15;
            Q15=makeQuery(id+"F1.opExtrude","SWEPT_FACE",FACE,{"disambiguationData":[OSD([sQuery(id+"F0.wireOp",EDGE,"E8.2.1.2")])]});
            var Q16;
            Q16=makeQuery(id+"F1.opExtrude","SWEPT_FACE",FACE,{"disambiguationData":[OSD([sQuery(id+"F0.wireOp",EDGE,"E8.3.1.2")])]});
            var Q17;
            Q17=makeQuery(id+"F1.opExtrude","SWEPT_FACE",FACE,{"disambiguationData":[OSD([sQuery(id+"F0.wireOp",EDGE,"E8.3.0.2")])]});
            var Q18;
            Q18=makeQuery(id+"F1.opExtrude","SWEPT_FACE",FACE,{"disambiguationData":[OSD([sQuery(id+"F0.wireOp",EDGE,"E8.2.0.2")])]});
            var Q19;
            Q19=makeQuery(id+"F1.opExtrude","SWEPT_FACE",FACE,{"disambiguationData":[OSD([sQuery(id+"F0.wireOp",EDGE,"E8.1.0.2")])]});
            var Q20;
            Q20=makeQuery(id+"F1.opExtrude","SWEPT_FACE",FACE,{"disambiguationData":[OSD([sQuery(id+"F0.wireOp",EDGE,"E8.1.3.0")])]});
            var Q21;
            Q21=makeQuery(id+"F1.opExtrude","SWEPT_FACE",FACE,{"disambiguationData":[OSD([sQuery(id+"F0.wireOp",EDGE,"E8.2.3.0")])]});
            var Q22;
            Q22=makeQuery(id+"F1.opExtrude","SWEPT_FACE",FACE,{"disambiguationData":[OSD([sQuery(id+"F0.wireOp",EDGE,"E8.3.3.0")])]});
            var Q23;
            Q23=makeQuery(id+"F1.opExtrude","SWEPT_FACE",FACE,{"disambiguationData":[OSD([sQuery(id+"F0.wireOp",EDGE,"E8.3.2.0")])]});
            var Q24;
            Q24=makeQuery(id+"F1.opExtrude","SWEPT_FACE",FACE,{"disambiguationData":[OSD([sQuery(id+"F0.wireOp",EDGE,"E8.2.2.0")])]});
            var Q25;
            Q25=makeQuery(id+"F1.opExtrude","SWEPT_FACE",FACE,{"disambiguationData":[OSD([sQuery(id+"F0.wireOp",EDGE,"E8.1.2.0")])]});
            var Q26;
            Q26=makeQuery(id+"F1.opExtrude","SWEPT_FACE",FACE,{"disambiguationData":[OSD([sQuery(id+"F0.wireOp",EDGE,"E8.1.1.0")])]});
            var Q27;
            Q27=makeQuery(id+"F1.opExtrude","SWEPT_FACE",FACE,{"disambiguationData":[OSD([sQuery(id+"F0.wireOp",EDGE,"E8.2.1.0")])]});
            var Q28;
            Q28=makeQuery(id+"F1.opExtrude","SWEPT_FACE",FACE,{"disambiguationData":[OSD([sQuery(id+"F0.wireOp",EDGE,"E8.3.1.0")])]});
            var Q29;
            Q29=makeQuery(id+"F1.opExtrude","SWEPT_FACE",FACE,{"disambiguationData":[OSD([sQuery(id+"F0.wireOp",EDGE,"E8.3.0.0")])]});
            var Q30;
            Q30=makeQuery(id+"F1.opExtrude","SWEPT_FACE",FACE,{"disambiguationData":[OSD([sQuery(id+"F0.wireOp",EDGE,"E8.2.0.0")])]});
            var Q31;
            Q31=makeQuery(id+"F1.opExtrude","SWEPT_FACE",FACE,{"disambiguationData":[OSD([sQuery(id+"F0.wireOp",EDGE,"E8.1.0.0")])]});
            chamfer(context, id + "F5", {"entities" : qUnion([Q0, Q1, Q2, Q3, Q4, Q5, Q6, Q7, Q8, Q9, Q10, Q11, Q12, Q13, Q14, Q15, Q16, Q17, Q18, Q19, Q20, Q21, Q22, Q23, Q24, Q25, Q26, Q27, Q28, Q29, Q30, Q31]), "width" : 0.5 * mm, "tangentPropagation" : true});
        }
    });
